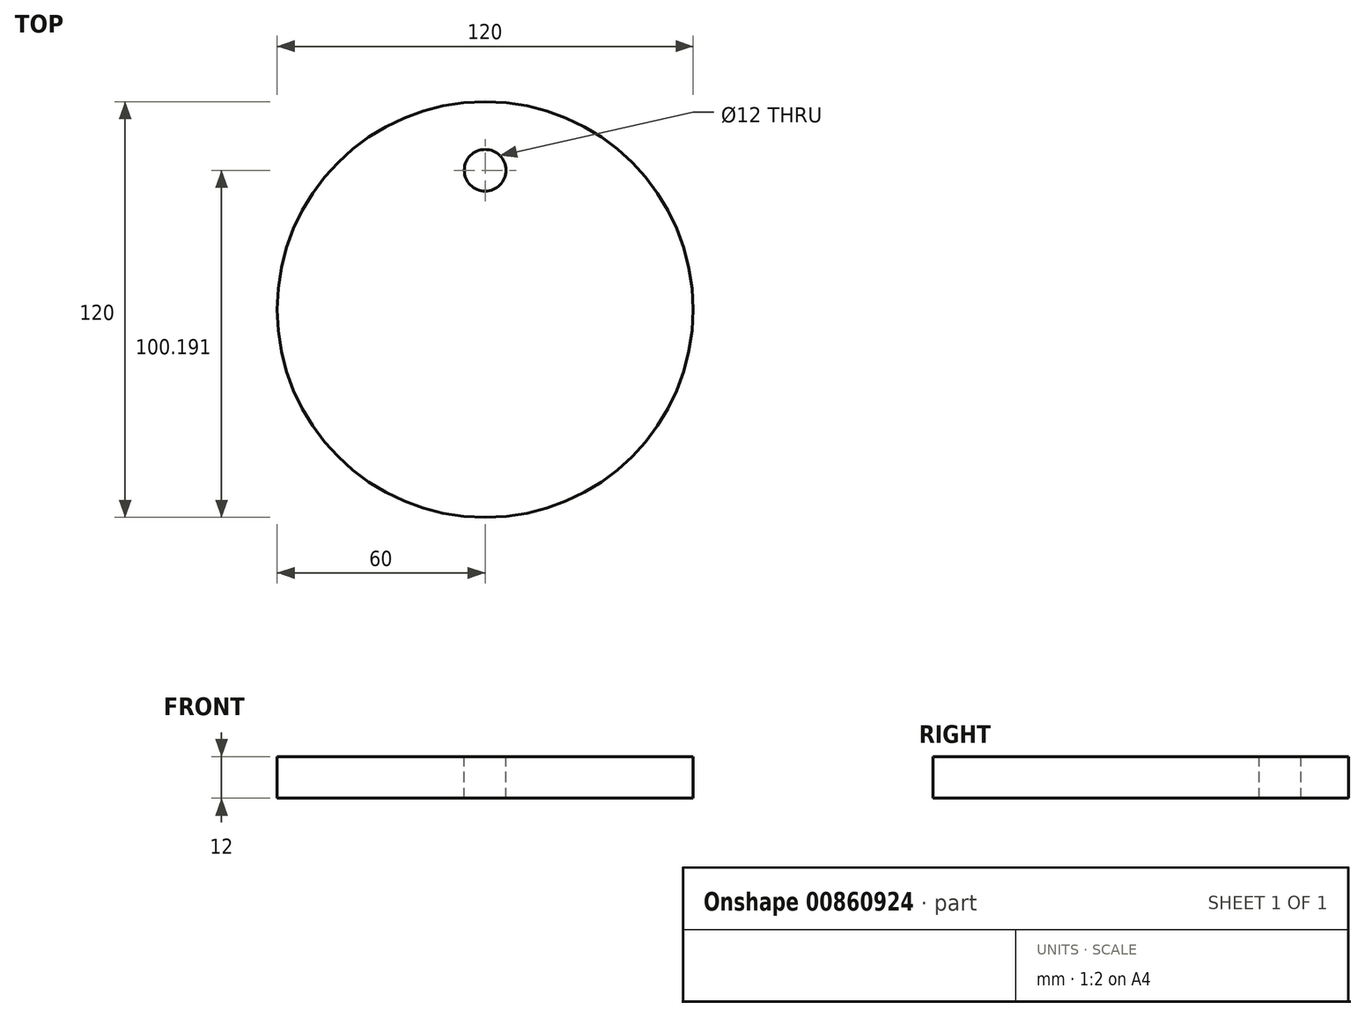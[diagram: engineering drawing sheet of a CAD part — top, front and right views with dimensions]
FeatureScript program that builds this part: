
annotation { "Feature Type Name" : "Feature", "Feature Type Description" : "" }
export const myFeature = defineFeature(function(context is Context, id is Id, definition is map)
    precondition{}
    {
        {
            assignVariable(context, id + "F0", {"name" : "bigcircle", "anyValue" : 120});
        }
        {
            assignVariable(context, id + "F1", {"name" : "thickness", "anyValue" : getVariable(context, 'bigcircle') / 10});
        }
        {
            var Q0;
            Q0=qCreatedBy(makeId("Top.planeOp"),FACE);
            var sketch = newSketch(context, id + "F2", { "sketchPlane" : qUnion([Q0])});
            skCircle(sketch, "E0", {"center": v(0, 0) * mm, "radius": 60 * mm});
            skSolve(sketch);
        }
        {
            var Q0;
            Q0=makeQuery(id+"F2.imprint","IMPRINT",FACE,{"disambiguationData":[TD([[makeQuery(id+"F2.imprint","IMPRINT",EDGE,{"derivedFrom":sQuery(id+"F2.wireOp",EDGE,"E0")}),1.0]])]});
            extrude(context, id + "F3", {"entities" : qUnion([Q0]), "depth" : (getVariable(context, 'thickness')) * mm, "offsetDistance" : 25 * mm});
        }
        {
            var Q0;
            Q0=makeQuery(id+"F3.opExtrude","CAP_FACE",FACE,{"disambiguationData":[OSD([sQuery(id+"F2.wireOp",EDGE,"E0")])],"isStart":false});
            var sketch = newSketch(context, id + "F4", { "sketchPlane" : qUnion([Q0])});
            skCircle(sketch, "E1", {"center": v(0, 0) * mm, "radius": 40 * mm, "construction": true});
            skSolve(sketch);
        }
        {
            var Q0;
            Q0=makeQuery(id+"F4.imprint","IMPRINT",FACE,{"disambiguationData":[TD([[makeQuery(id+"F4.imprint","IMPRINT",EDGE,{"derivedFrom":makeQuery(id+"F3.opExtrude","CAP_EDGE",EDGE,{"disambiguationData":[OSD([sQuery(id+"F2.wireOp",EDGE,"E0")])],"isStart":false})}),1.0]])]});
            var sketch = newSketch(context, id + "F5", { "sketchPlane" : qUnion([Q0])});
            skCircle(sketch, "E2", {"center": v(0, 40.2) * mm, "radius": 6 * mm});
            skSolve(sketch);
        }
        {
            var Q0;
            Q0 = qSketchRegion(id + "F5", true);
            extrude(context, id + "F6", {"entities" : qUnion([Q0]), "operationType" : NewBodyOperationType.REMOVE, "endBound" : BoundingType.THROUGH_ALL, "oppositeDirection" : true, "depth" : 25 * mm, "offsetDistance" : 25 * mm});
        }
    });
